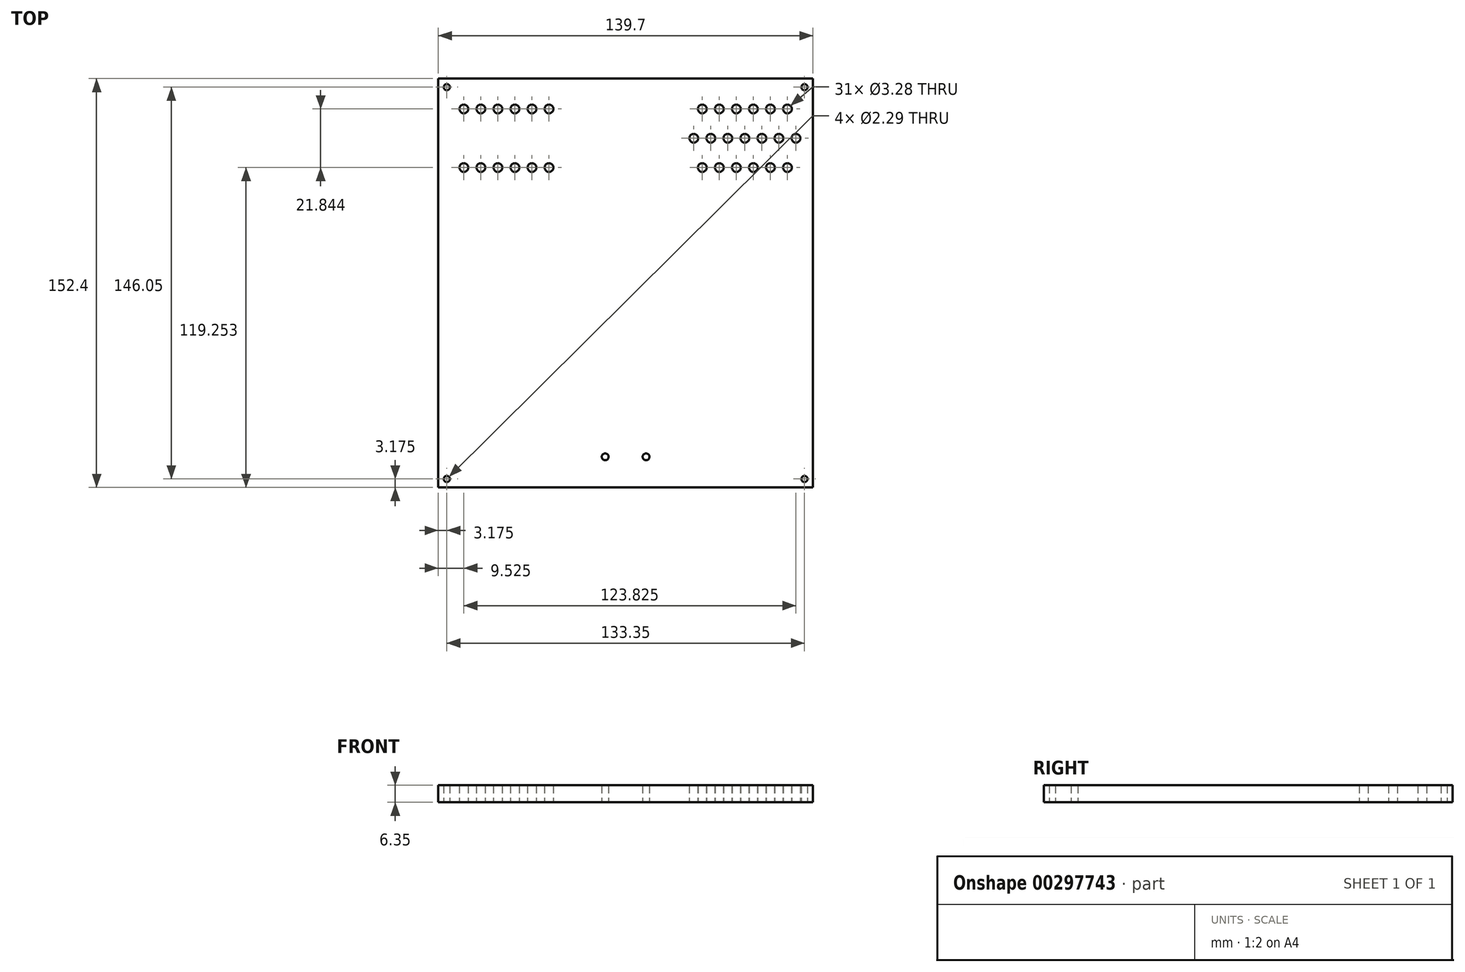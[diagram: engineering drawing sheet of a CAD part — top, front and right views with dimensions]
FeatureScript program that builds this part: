
annotation { "Feature Type Name" : "Feature", "Feature Type Description" : "" }
export const myFeature = defineFeature(function(context is Context, id is Id, definition is map)
    precondition{}
    {
        {
            var Q0;
            Q0=qCreatedBy(makeId("Top.planeOp"),FACE);
            var sketch = newSketch(context, id + "F0", { "sketchPlane" : qUnion([Q0])});
            skLineSegment(sketch, "E0.bottom", {"start": v(-69.85, 76.2) * mm, "end": v(69.85, 76.2) * mm});
            skLineSegment(sketch, "E0.top", {"start": v(-69.85, -76.2) * mm, "end": v(69.85, -76.2) * mm});
            skLineSegment(sketch, "E0.left", {"start": v(-69.85, 76.2) * mm, "end": v(-69.85, -76.2) * mm});
            skLineSegment(sketch, "E0.right", {"start": v(69.85, 76.2) * mm, "end": v(69.85, -76.2) * mm});
            skPoint(sketch, "E0.middle", {"position": v(0, 0) * mm});
            skLineSegment(sketch, "E1", {"start": v(-69.85, 73.03) * mm, "end": v(-66.68, 73.03) * mm, "construction": true});
            skLineSegment(sketch, "E2", {"start": v(-66.68, 73.03) * mm, "end": v(-66.68, 76.2) * mm, "construction": true});
            skCircle(sketch, "E3", {"center": v(-66.68, 73.03) * mm, "radius": 1.14 * mm});
            skCircle(sketch, "E4.MirrorC", {"center": v(-66.68, -73.03) * mm, "radius": 1.14 * mm});
            skCircle(sketch, "E5.MirrorC", {"center": v(66.68, -73.03) * mm, "radius": 1.14 * mm});
            skCircle(sketch, "E6.MirrorC", {"center": v(66.68, 73.03) * mm, "radius": 1.14 * mm});
            skLineSegment(sketch, "E7", {"start": v(-66.68, 73.03) * mm, "end": v(-66.68, 34.93) * mm, "construction": true});
            skPoint(sketch, "E8.endSnap0", {"position": v(-66.68, 53.98) * mm});
            skLineSegment(sketch, "E9", {"start": v(-69.85, 53.98) * mm, "end": v(-19.05, 53.98) * mm, "construction": true});
            skCircle(sketch, "E10", {"center": v(-44.45, 53.98) * mm, "radius": 1.64 * mm});
            skCircle(sketch, "E11.MirrorC", {"center": v(44.45, 53.98) * mm, "radius": 1.64 * mm});
            skCircle(sketch, "E12.1.0.0", {"center": v(-38.1, 53.98) * mm, "radius": 1.64 * mm});
            skCircle(sketch, "E12.2.0.0", {"center": v(-31.75, 53.98) * mm, "radius": 1.64 * mm});
            skCircle(sketch, "E12.3.0.0", {"center": v(-25.4, 53.98) * mm, "radius": 1.64 * mm});
            skLineSegment(sketch, "E12.direction1", {"start": v(-44.45, 53.98) * mm, "end": v(-38.1, 53.98) * mm, "construction": true});
            skCircle(sketch, "E13.1.0.0", {"center": v(-50.8, 53.98) * mm, "radius": 1.64 * mm});
            skCircle(sketch, "E13.2.0.0", {"center": v(-57.15, 53.98) * mm, "radius": 1.64 * mm});
            skCircle(sketch, "E13.3.0.0", {"center": v(-63.5, 53.98) * mm, "radius": 1.64 * mm});
            skLineSegment(sketch, "E13.direction1", {"start": v(-44.45, 53.98) * mm, "end": v(-50.8, 53.98) * mm, "construction": true});
            skCircle(sketch, "E14.MirrorC", {"center": v(25.4, 53.98) * mm, "radius": 1.64 * mm});
            skCircle(sketch, "E15.MirrorC", {"center": v(31.75, 53.98) * mm, "radius": 1.64 * mm});
            skCircle(sketch, "E16.MirrorC", {"center": v(38.1, 53.98) * mm, "radius": 1.64 * mm});
            skCircle(sketch, "E17.MirrorC", {"center": v(50.8, 53.98) * mm, "radius": 1.64 * mm});
            skCircle(sketch, "E18.MirrorC", {"center": v(57.15, 53.98) * mm, "radius": 1.64 * mm});
            skCircle(sketch, "E19.MirrorC", {"center": v(63.5, 53.98) * mm, "radius": 1.64 * mm});
            skLineSegment(sketch, "E20", {"start": v(-41.28, 53.98) * mm, "end": v(-41.28, 64.9) * mm, "construction": true});
            skCircle(sketch, "E21", {"center": v(-41.28, 64.9) * mm, "radius": 1.64 * mm});
            skCircle(sketch, "E22.1.0.0", {"center": v(-34.93, 64.9) * mm, "radius": 1.64 * mm});
            skCircle(sketch, "E22.2.0.0", {"center": v(-28.58, 64.9) * mm, "radius": 1.64 * mm});
            skLineSegment(sketch, "E22.direction1", {"start": v(-41.28, 64.9) * mm, "end": v(-34.93, 64.9) * mm, "construction": true});
            skCircle(sketch, "E23.1.0.0", {"center": v(-47.63, 64.9) * mm, "radius": 1.64 * mm});
            skCircle(sketch, "E23.2.0.0", {"center": v(-53.98, 64.9) * mm, "radius": 1.64 * mm});
            skLineSegment(sketch, "E23.direction1", {"start": v(-41.28, 64.9) * mm, "end": v(-47.63, 64.9) * mm, "construction": true});
            skCircle(sketch, "E24.0.3.0", {"center": v(-60.33, 64.9) * mm, "radius": 1.64 * mm});
            skCircle(sketch, "E25.MirrorC", {"center": v(-28.58, 43.05) * mm, "radius": 1.64 * mm});
            skCircle(sketch, "E26.MirrorC", {"center": v(-34.93, 43.05) * mm, "radius": 1.64 * mm});
            skCircle(sketch, "E27.MirrorC", {"center": v(-41.28, 43.05) * mm, "radius": 1.64 * mm});
            skCircle(sketch, "E28.MirrorC", {"center": v(-47.63, 43.05) * mm, "radius": 1.64 * mm});
            skCircle(sketch, "E29.MirrorC", {"center": v(-53.98, 43.05) * mm, "radius": 1.64 * mm});
            skCircle(sketch, "E30.MirrorC", {"center": v(-60.33, 43.05) * mm, "radius": 1.64 * mm});
            skCircle(sketch, "E31.MirrorC", {"center": v(60.33, 43.05) * mm, "radius": 1.64 * mm});
            skCircle(sketch, "E32.MirrorC", {"center": v(53.98, 43.05) * mm, "radius": 1.64 * mm});
            skCircle(sketch, "E33.MirrorC", {"center": v(47.63, 43.05) * mm, "radius": 1.64 * mm});
            skCircle(sketch, "E34.MirrorC", {"center": v(41.28, 43.05) * mm, "radius": 1.64 * mm});
            skCircle(sketch, "E35.MirrorC", {"center": v(34.93, 43.05) * mm, "radius": 1.64 * mm});
            skCircle(sketch, "E36.MirrorC", {"center": v(28.58, 43.05) * mm, "radius": 1.64 * mm});
            skCircle(sketch, "E37.MirrorC", {"center": v(28.58, 64.9) * mm, "radius": 1.64 * mm});
            skCircle(sketch, "E38.MirrorC", {"center": v(34.93, 64.9) * mm, "radius": 1.64 * mm});
            skCircle(sketch, "E39.MirrorC", {"center": v(41.28, 64.9) * mm, "radius": 1.64 * mm});
            skCircle(sketch, "E40.MirrorC", {"center": v(47.63, 64.9) * mm, "radius": 1.64 * mm});
            skCircle(sketch, "E41.MirrorC", {"center": v(53.98, 64.9) * mm, "radius": 1.64 * mm});
            skCircle(sketch, "E42.MirrorC", {"center": v(60.33, 64.9) * mm, "radius": 1.64 * mm});
            skLineSegment(sketch, "E43", {"start": v(0, -76.2) * mm, "end": v(0, -64.77) * mm, "construction": true});
            skPoint(sketch, "E43.endSnap0", {"position": v(0, -76.2) * mm});
            skLineSegment(sketch, "E44", {"start": v(-7.62, -64.77) * mm, "end": v(7.62, -64.77) * mm, "construction": true});
            skCircle(sketch, "E45", {"center": v(-7.62, -64.77) * mm, "radius": 1.27 * mm});
            skCircle(sketch, "E46", {"center": v(7.62, -64.77) * mm, "radius": 1.27 * mm});
            skSolve(sketch);
        }
        {
            var Q0;
            Q0=makeQuery(id+"F0.imprint","IMPRINT",FACE,{"disambiguationData":[TD([[makeQuery(id+"F0.imprint","IMPRINT",EDGE,{"derivedFrom":sQuery(id+"F0.wireOp",EDGE,"E0.bottom")}),-1.0]])]});
            var Q1;
            Q1=makeQuery(id+"F0.imprint","IMPRINT",FACE,{"disambiguationData":[TD([[makeQuery(id+"F0.imprint","IMPRINT",EDGE,{"derivedFrom":sQuery(id+"F0.wireOp",EDGE,"E13.3.0.0")}),1.0]])]});
            var Q2;
            Q2=makeQuery(id+"F0.imprint","IMPRINT",FACE,{"disambiguationData":[TD([[makeQuery(id+"F0.imprint","IMPRINT",EDGE,{"derivedFrom":sQuery(id+"F0.wireOp",EDGE,"E13.2.0.0")}),1.0]])]});
            var Q3;
            Q3=makeQuery(id+"F0.imprint","IMPRINT",FACE,{"disambiguationData":[TD([[makeQuery(id+"F0.imprint","IMPRINT",EDGE,{"derivedFrom":sQuery(id+"F0.wireOp",EDGE,"E13.1.0.0")}),1.0]])]});
            var Q4;
            Q4=makeQuery(id+"F0.imprint","IMPRINT",FACE,{"disambiguationData":[TD([[makeQuery(id+"F0.imprint","IMPRINT",EDGE,{"derivedFrom":sQuery(id+"F0.wireOp",EDGE,"E10")}),1.0]])]});
            var Q5;
            Q5=makeQuery(id+"F0.imprint","IMPRINT",FACE,{"disambiguationData":[TD([[makeQuery(id+"F0.imprint","IMPRINT",EDGE,{"derivedFrom":sQuery(id+"F0.wireOp",EDGE,"E12.1.0.0")}),1.0]])]});
            var Q6;
            Q6=makeQuery(id+"F0.imprint","IMPRINT",FACE,{"disambiguationData":[TD([[makeQuery(id+"F0.imprint","IMPRINT",EDGE,{"derivedFrom":sQuery(id+"F0.wireOp",EDGE,"E12.2.0.0")}),1.0]])]});
            var Q7;
            Q7=makeQuery(id+"F0.imprint","IMPRINT",FACE,{"disambiguationData":[TD([[makeQuery(id+"F0.imprint","IMPRINT",EDGE,{"derivedFrom":sQuery(id+"F0.wireOp",EDGE,"E12.3.0.0")}),1.0]])]});
            var Q8;
            Q8=makeQuery(id+"F0.imprint","IMPRINT",FACE,{"disambiguationData":[TD([[makeQuery(id+"F0.imprint","IMPRINT",EDGE,{"derivedFrom":sQuery(id+"F0.wireOp",EDGE,"E19.MirrorC")}),-1.0]])]});
            var Q9;
            Q9=makeQuery(id+"F0.imprint","IMPRINT",FACE,{"disambiguationData":[TD([[makeQuery(id+"F0.imprint","IMPRINT",EDGE,{"derivedFrom":sQuery(id+"F0.wireOp",EDGE,"E18.MirrorC")}),-1.0]])]});
            var Q10;
            Q10=makeQuery(id+"F0.imprint","IMPRINT",FACE,{"disambiguationData":[TD([[makeQuery(id+"F0.imprint","IMPRINT",EDGE,{"derivedFrom":sQuery(id+"F0.wireOp",EDGE,"E17.MirrorC")}),-1.0]])]});
            var Q11;
            Q11=makeQuery(id+"F0.imprint","IMPRINT",FACE,{"disambiguationData":[TD([[makeQuery(id+"F0.imprint","IMPRINT",EDGE,{"derivedFrom":sQuery(id+"F0.wireOp",EDGE,"E11.MirrorC")}),-1.0]])]});
            var Q12;
            Q12=makeQuery(id+"F0.imprint","IMPRINT",FACE,{"disambiguationData":[TD([[makeQuery(id+"F0.imprint","IMPRINT",EDGE,{"derivedFrom":sQuery(id+"F0.wireOp",EDGE,"E16.MirrorC")}),-1.0]])]});
            var Q13;
            Q13=makeQuery(id+"F0.imprint","IMPRINT",FACE,{"disambiguationData":[TD([[makeQuery(id+"F0.imprint","IMPRINT",EDGE,{"derivedFrom":sQuery(id+"F0.wireOp",EDGE,"E15.MirrorC")}),-1.0]])]});
            var Q14;
            Q14=makeQuery(id+"F0.imprint","IMPRINT",FACE,{"disambiguationData":[TD([[makeQuery(id+"F0.imprint","IMPRINT",EDGE,{"derivedFrom":sQuery(id+"F0.wireOp",EDGE,"E14.MirrorC")}),-1.0]])]});
            extrude(context, id + "F1", {"entities" : qUnion([Q0, Q1, Q2, Q3, Q4, Q5, Q6, Q7, Q8, Q9, Q10, Q11, Q12, Q13, Q14]), "depth" : 6.35 * mm});
        }
    });
